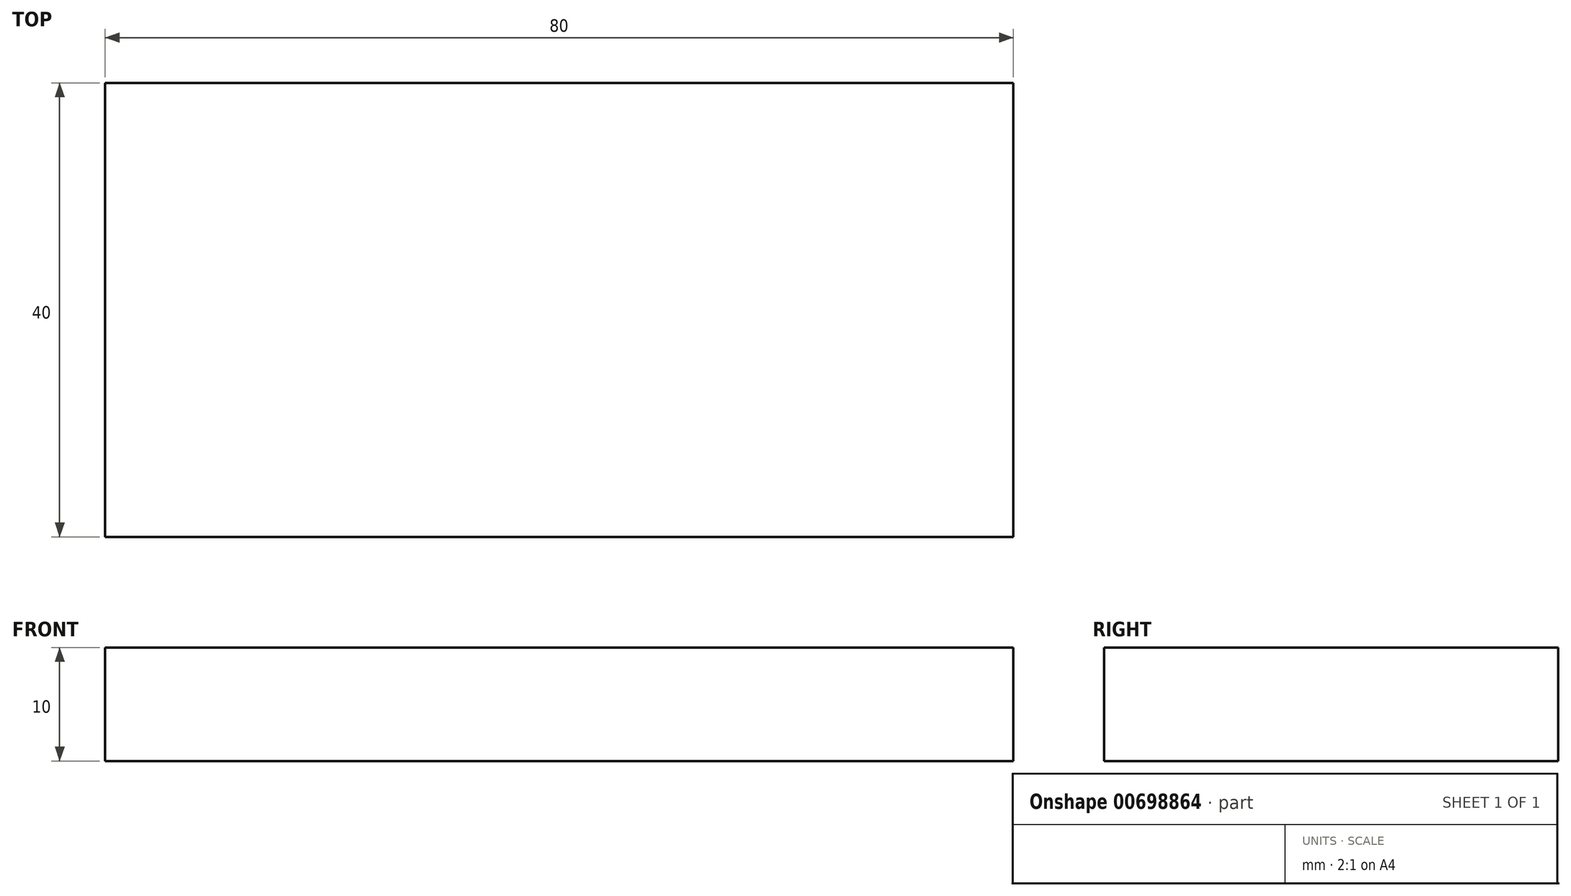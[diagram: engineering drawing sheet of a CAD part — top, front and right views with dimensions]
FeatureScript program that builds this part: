
annotation { "Feature Type Name" : "Feature", "Feature Type Description" : "" }
export const myFeature = defineFeature(function(context is Context, id is Id, definition is map)
    precondition{}
    {
        {
            var Q0;
            Q0=qCreatedBy(makeId("Top.planeOp"),FACE);
            var sketch = newSketch(context, id + "F0", { "sketchPlane" : qUnion([Q0])});
            skLineSegment(sketch, "E0.bottom", {"start": v(-80, 40) * mm, "end": v(0, 40) * mm});
            skLineSegment(sketch, "E0.top", {"start": v(-80, 0) * mm, "end": v(0, 0) * mm});
            skLineSegment(sketch, "E0.left", {"start": v(-80, 40) * mm, "end": v(-80, 0) * mm});
            skLineSegment(sketch, "E0.right", {"start": v(0, 40) * mm, "end": v(0, 0) * mm});
            skSolve(sketch);
        }
        {
            var Q0;
            Q0 = qSketchRegion(id + "F0", true);
            extrude(context, id + "F1", {"entities" : qUnion([Q0]), "depth" : 10 * mm, "offsetDistance" : 25.4 * mm});
        }
    });
